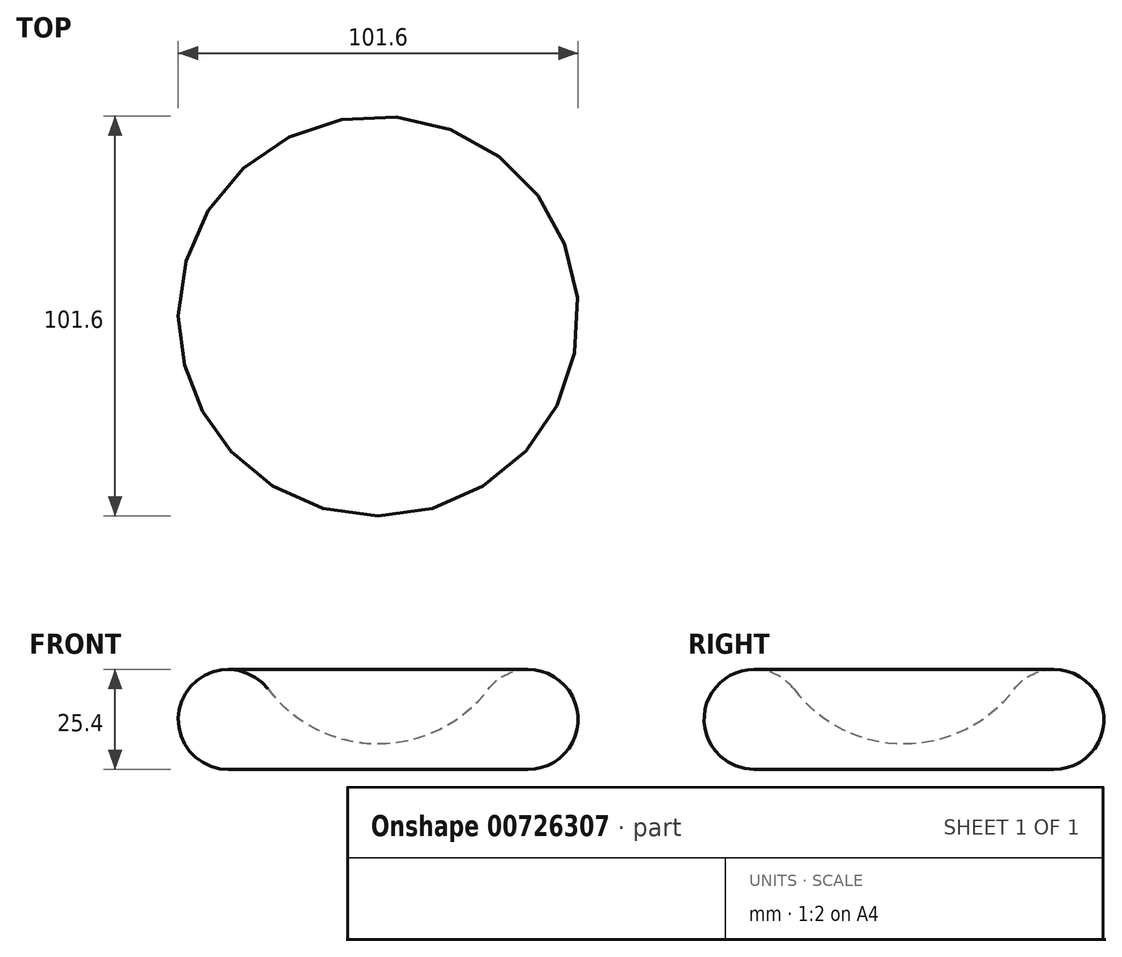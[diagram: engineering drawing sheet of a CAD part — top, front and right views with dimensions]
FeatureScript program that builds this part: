
annotation { "Feature Type Name" : "Feature", "Feature Type Description" : "" }
export const myFeature = defineFeature(function(context is Context, id is Id, definition is map)
    precondition{}
    {
        {
            var Q0;
            Q0=qCreatedBy(makeId("Front.planeOp"),FACE);
            var sketch = newSketch(context, id + "F0", { "sketchPlane" : qUnion([Q0])});
            skArc(sketch, "E0", {"start": v(-28, 20.41) * mm, "mid": v(-49.48, 18.33) * mm, "end": v(-38.1, 0) * mm});
            skArc(sketch, "E1", {"start": v(-28, 20.41) * mm, "mid": v(-15.62, 10.21) * mm, "end": v(0, 6.56) * mm});
            skLineSegment(sketch, "E2", {"start": v(-38.1, 0) * mm, "end": v(0, 0) * mm});
            skLineSegment(sketch, "E3", {"start": v(0, 0) * mm, "end": v(0, 6.56) * mm});
            skSolve(sketch);
        }
        {
            var Q0;
            Q0=makeQuery(id+"F0.imprint","IMPRINT",FACE,{"disambiguationData":[TD([[makeQuery(id+"F0.imprint","IMPRINT",EDGE,{"derivedFrom":sQuery(id+"F0.wireOp",EDGE,"E0")}),1.0]])]});
            var Q1;
            Q1=sQuery(id+"F0.wireOp",EDGE,"E3");
            revolve(context, id + "F1", {"surfaceOperationType" : NewSurfaceOperationType.NEW, "entities" : qUnion([Q0]), "axis" : qUnion([Q1]), "revolveType" : RevolveType.FULL});
        }
        {
            var Q0;
            Q0=qCreatedBy(makeId("Top.planeOp"),FACE);
            cPlane(context, id + "F2", {"entities" : qUnion([Q0]), "cplaneType" : CPlaneType.OFFSET, "offset" : 25.4 * mm, "width" : 152.4 * mm, "height" : 152.4 * mm});
        }
    });
